# Revit family: f606847e-12c4-483e-a721-5344f737bcba
name_source: partatom
category: Specialty Equipment
revit_build: Autodesk Revit 2016 (Build: 20161004_0715(x64)
units: mm (PartAtom-declared; Revit-internal decimal feet)

## family parameters
Always vertical = Yes
Cut with Voids When Loaded = No
OmniClass Number = 23.35.70.24.11.11
OmniClass Title = Suspended Ceiling Components
Part Type = Normal
Room Calculation Point = No
Round Connector Dimension = Use Diameter
Shared = No
Work Plane-Based = No

## types (1)
- Unistrut_Main
    04 CSI = 09 51 00
    95 CSI = 09510
    Assembly Code = C3030200
    Carrier Visibility = Yes
    Default Elevation = 0"
    Description = Upper_Clip
    Manufacturer = Hunter Douglas Luxalon Metal Ceilings
    Model = Natura Wall Upper_Clip
    Product Line = Natura Wall
    Subcategory = Natura Wood
    URL = http://www.hunterdouglascontract.com
    Unit = Metal - Aluminum Frame - HunterDouglas - Painted White

## geometry (parser evidence)
native form markers: Sweep x5
no freeform markers — native parametric forms only
